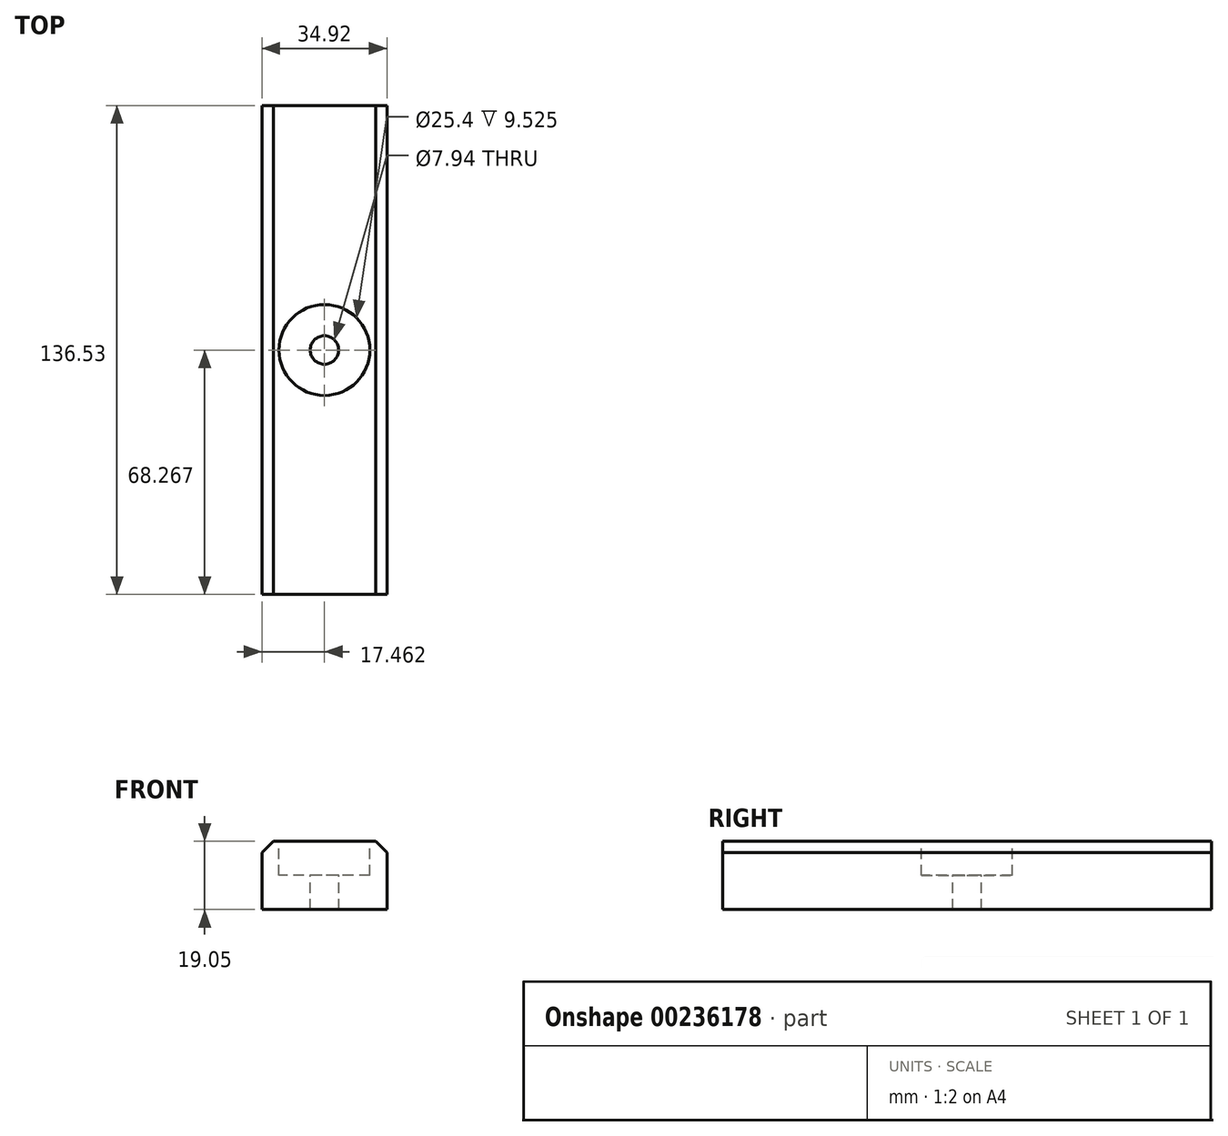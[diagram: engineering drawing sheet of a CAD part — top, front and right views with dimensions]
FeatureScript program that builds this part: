
annotation { "Feature Type Name" : "Feature", "Feature Type Description" : "" }
export const myFeature = defineFeature(function(context is Context, id is Id, definition is map)
    precondition{}
    {
        {
            var Q0;
            Q0=qCreatedBy(makeId("Front.planeOp"),FACE);
            var sketch = newSketch(context, id + "F0", { "sketchPlane" : qUnion([Q0])});
            skLineSegment(sketch, "E0", {"start": v(0, 0) * mm, "end": v(0, -19.05) * mm});
            skLineSegment(sketch, "E1", {"start": v(0, -19.05) * mm, "end": v(34.93, -19.05) * mm});
            skLineSegment(sketch, "E2", {"start": v(34.93, -19.05) * mm, "end": v(34.93, 0) * mm});
            skLineSegment(sketch, "E3", {"start": v(34.93, 0) * mm, "end": v(0, 0) * mm});
            skSolve(sketch);
        }
        {
            var Q0;
            Q0 = qSketchRegion(id + "F0", true);
            extrude(context, id + "F1", {"entities" : qUnion([Q0]), "depth" : 136.53 * mm});
        }
        {
            var Q0;
            Q0=makeQuery(id+"F1.opExtrude","SWEPT_EDGE",EDGE,{"disambiguationData":[OSD([sQuery(id+"F0.wireOp",EDGE,"E2"),sQuery(id+"F0.wireOp",EDGE,"E3")])]});
            var Q1;
            Q1=makeQuery(id+"F1.opExtrude","SWEPT_EDGE",EDGE,{"disambiguationData":[OSD([sQuery(id+"F0.wireOp",EDGE,"E0"),sQuery(id+"F0.wireOp",EDGE,"E3")])]});
            chamfer(context, id + "F2", {"entities" : qUnion([Q0, Q1]), "width" : 3.17 * mm, "tangentPropagation" : true});
        }
        {
            var Q0;
            Q0=makeQuery(id+"F1.opExtrude","SWEPT_FACE",FACE,{"disambiguationData":[OSD([sQuery(id+"F0.wireOp",EDGE,"E3")])]});
            var sketch = newSketch(context, id + "F3", { "sketchPlane" : qUnion([Q0])});
            skCircle(sketch, "E4", {"center": v(17.46, -68.26) * mm, "radius": 12.7 * mm});
            skPoint(sketch, "E4.centerSnap0", {"position": v(17.46, 0) * mm});
            skPoint(sketch, "E4.centerSnap1", {"position": v(3.18, -68.26) * mm});
            skSolve(sketch);
        }
        {
            var Q0;
            Q0=makeQuery(id+"F3.imprint","IMPRINT",FACE,{"disambiguationData":[TD([[makeQuery(id+"F3.imprint","IMPRINT",EDGE,{"derivedFrom":sQuery(id+"F3.wireOp",EDGE,"E4")}),1.0]])]});
            extrude(context, id + "F4", {"entities" : qUnion([Q0]), "operationType" : NewBodyOperationType.REMOVE, "oppositeDirection" : true, "depth" : 9.52 * mm});
        }
        {
            var Q0;
            Q0=makeQuery(id+"F4.boolean.opBoolean","COPY",FACE,{"derivedFrom":makeQuery(id+"F4.opExtrude","CAP_FACE",FACE,{"disambiguationData":[OSD([sQuery(id+"F3.wireOp",EDGE,"E4")])],"isStart":false})});
            var sketch = newSketch(context, id + "F5", { "sketchPlane" : qUnion([Q0])});
            skCircle(sketch, "E5", {"center": v(17.46, -68.26) * mm, "radius": 3.97 * mm});
            skSolve(sketch);
        }
        {
            var Q0;
            Q0=makeQuery(id+"F5.imprint","IMPRINT",FACE,{"disambiguationData":[TD([[makeQuery(id+"F5.imprint","IMPRINT",EDGE,{"derivedFrom":sQuery(id+"F5.wireOp",EDGE,"E5")}),1.0]])]});
            extrude(context, id + "F6", {"entities" : qUnion([Q0]), "operationType" : NewBodyOperationType.REMOVE, "oppositeDirection" : true, "depth" : 254 * mm});
        }
    });
